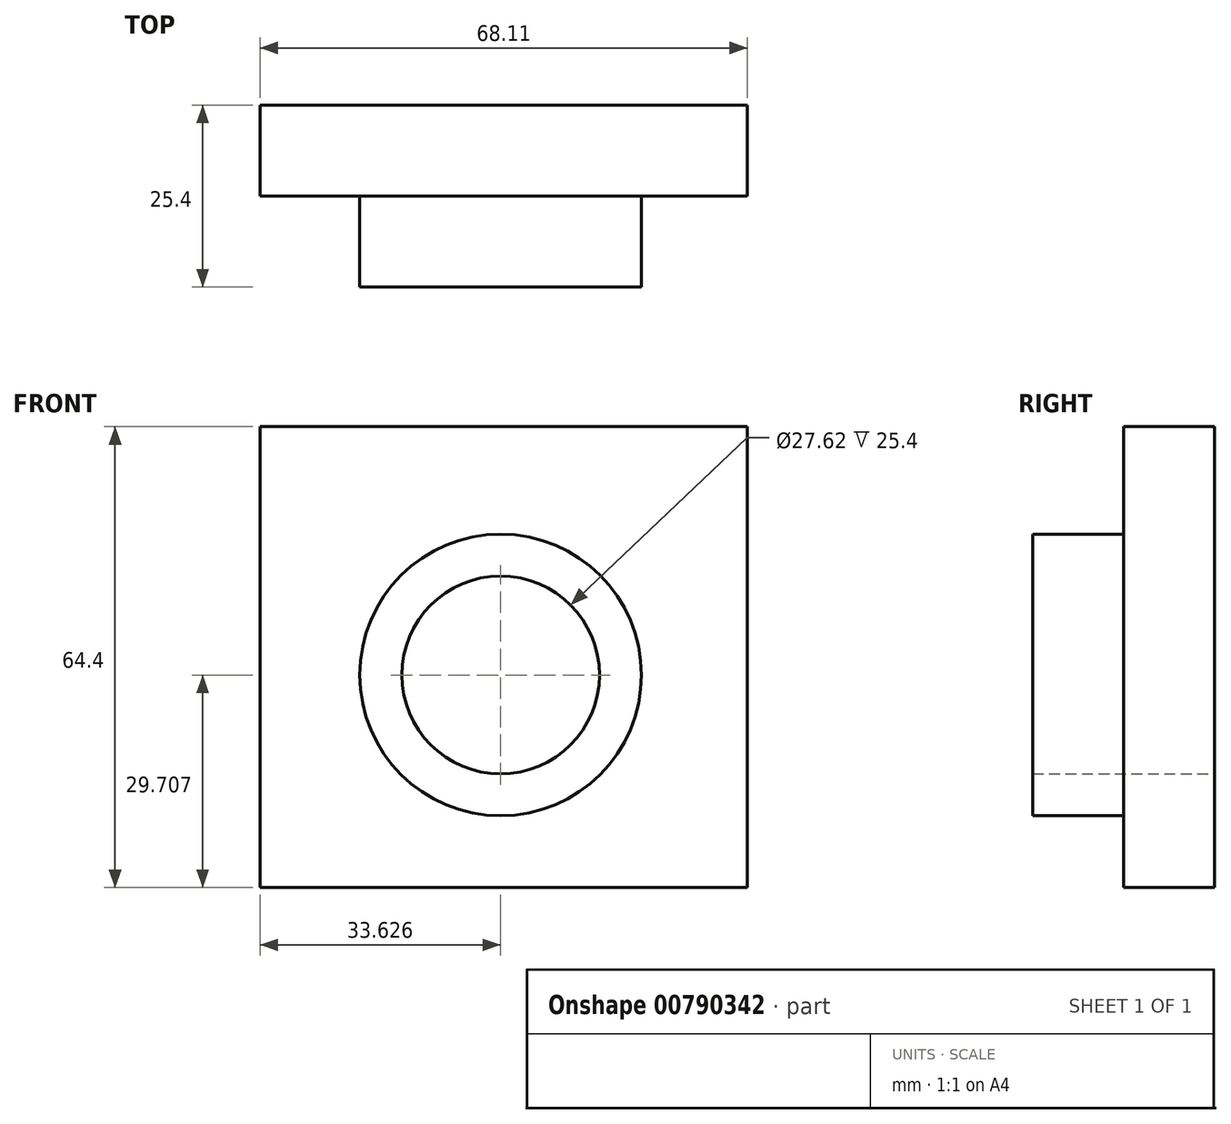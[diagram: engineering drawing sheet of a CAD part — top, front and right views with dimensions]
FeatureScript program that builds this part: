
annotation { "Feature Type Name" : "Feature", "Feature Type Description" : "" }
export const myFeature = defineFeature(function(context is Context, id is Id, definition is map)
    precondition{}
    {
        {
            var Q0;
            Q0=qCreatedBy(makeId("Front.planeOp"),FACE);
            var sketch = newSketch(context, id + "F0", { "sketchPlane" : qUnion([Q0])});
            skLineSegment(sketch, "E0.bottom", {"start": v(-29.1, 38.37) * mm, "end": v(39.01, 38.37) * mm});
            skLineSegment(sketch, "E0.top", {"start": v(-29.1, -26.03) * mm, "end": v(39.01, -26.03) * mm});
            skLineSegment(sketch, "E0.left", {"start": v(-29.1, 38.37) * mm, "end": v(-29.1, -26.03) * mm});
            skLineSegment(sketch, "E0.right", {"start": v(39.01, 38.37) * mm, "end": v(39.01, -26.03) * mm});
            skCircle(sketch, "E1", {"center": v(4.53, 3.68) * mm, "radius": 19.68 * mm});
            skCircle(sketch, "E2", {"center": v(4.53, 3.68) * mm, "radius": 13.81 * mm});
            skSolve(sketch);
        }
        {
            var Q0;
            Q0=makeQuery(id+"F0.imprint","IMPRINT",FACE,{"disambiguationData":[TD([[makeQuery(id+"F0.imprint","IMPRINT",EDGE,{"derivedFrom":sQuery(id+"F0.wireOp",EDGE,"E1")}),1.0]])]});
            extrude(context, id + "F1", {"entities" : qUnion([Q0]), "depth" : 25.4 * mm, "offsetDistance" : 25.4 * mm});
        }
        {
            var Q0;
            Q0=makeQuery(id+"F0.imprint","IMPRINT",FACE,{"disambiguationData":[TD([[makeQuery(id+"F0.imprint","IMPRINT",EDGE,{"derivedFrom":sQuery(id+"F0.wireOp",EDGE,"E0.bottom")}),-1.0]])]});
            extrude(context, id + "F2", {"entities" : qUnion([Q0]), "operationType" : NewBodyOperationType.ADD, "depth" : 12.7 * mm, "offsetDistance" : 25.4 * mm});
        }
    });
